# Revit family: AC-S6T - Yoke Mount
name_source: partatom
category: Generic Models
revit_build: Autodesk Revit 2014 (Build: 20130308_1515(x64)
units: mm (PartAtom-declared; Revit-internal decimal feet)

## types (1)
- AC-S6T - Yoke Mount
    100V Taps = 30, 15, 7.5 3.8
    70V Taps = 30, 15, 7.5, 3.7, 1.9
    Coverage Horizontal = 130.00°
    Coverage Vertical = 130.00°
    Default Elevation = 8' - 0"
    Depth = 0' - 11 23/32"
    Description = 6.5" 2-Way Surface Mount Loudspeaker
    Height = 1' - 11 15/32"
    Impedance = 8
    Manufacturer = QSC Audio Products, LLC
    Manufacturer URL = www.qsc.com
    Model = AC-S6T
    Mount Depth = 0' - 10"
    Mount Height = 1' - 11 17/32"
    Mount Width = 0' - 4 17/32"
    Power Handling = 30
    Product Documentation Link = TBA
    Product Page URL = TBA
    Regulatory Compliance = RoHS
    SPL Max = 107
    Sensitivity = 86
    URL = TBA
    Weight Dimensional (kg) = 8.4
    Weight Dimensional (lb) = 18.6
    Weight Product (kg) = 3.8
    Weight Product (lb) = 8.3
    Width = 0' - 8 1/2"

## geometry (parser evidence)
native form markers: Blend x2, Sweep x9
no freeform markers — native parametric forms only
